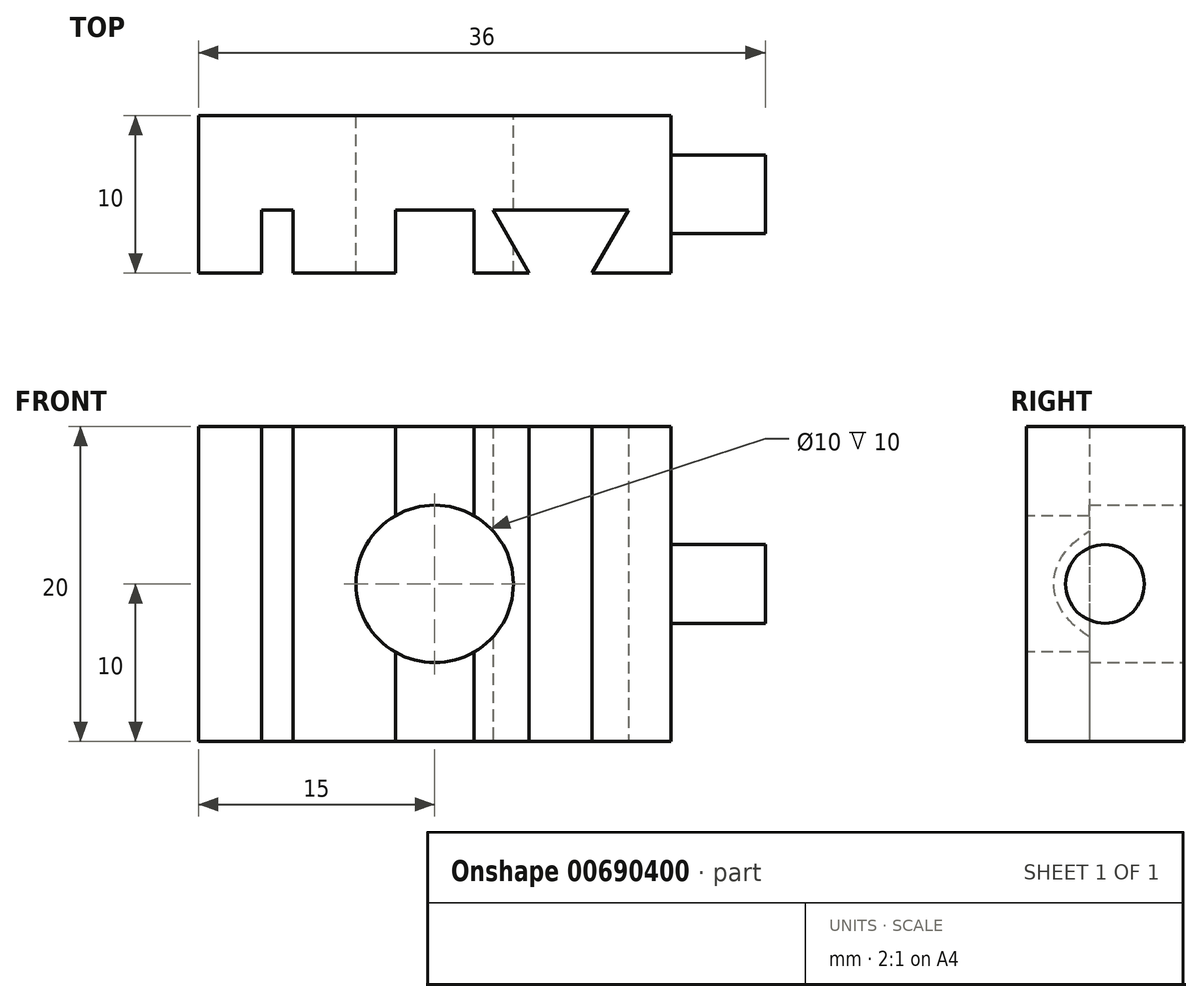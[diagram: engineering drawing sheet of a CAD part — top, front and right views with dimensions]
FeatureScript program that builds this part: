
annotation { "Feature Type Name" : "Feature", "Feature Type Description" : "" }
export const myFeature = defineFeature(function(context is Context, id is Id, definition is map)
    precondition{}
    {
        {
            var Q0;
            Q0=qCreatedBy(makeId("Front.planeOp"),FACE);
            var sketch = newSketch(context, id + "F0", { "sketchPlane" : qUnion([Q0])});
            skLineSegment(sketch, "E0.bottom", {"start": v(15, -10) * mm, "end": v(-15, -10) * mm});
            skLineSegment(sketch, "E0.top", {"start": v(15, 10) * mm, "end": v(-15, 10) * mm});
            skLineSegment(sketch, "E0.left", {"start": v(15, -10) * mm, "end": v(15, 10) * mm});
            skLineSegment(sketch, "E0.right", {"start": v(-15, -10) * mm, "end": v(-15, 10) * mm});
            skPoint(sketch, "E0.middle", {"position": v(0, 0) * mm});
            skCircle(sketch, "E1", {"center": v(0, 0) * mm, "radius": 5 * mm});
            skSolve(sketch);
        }
        {
            var Q0;
            Q0=makeQuery(id+"F0.imprint","IMPRINT",FACE,{"disambiguationData":[TD([[makeQuery(id+"F0.imprint","IMPRINT",EDGE,{"derivedFrom":sQuery(id+"F0.wireOp",EDGE,"E0.bottom")}),-1.0]])]});
            extrude(context, id + "F1", {"entities" : qUnion([Q0]), "depth" : 10 * mm, "offsetDistance" : 25 * mm});
        }
        {
            var Q0;
            Q0=makeQuery(id+"F1.opExtrude","CAP_FACE",FACE,{"disambiguationData":[OSD([sQuery(id+"F0.wireOp",EDGE,"E0.bottom"),sQuery(id+"F0.wireOp",EDGE,"E0.top"),sQuery(id+"F0.wireOp",EDGE,"E0.left"),sQuery(id+"F0.wireOp",EDGE,"E0.right"),sQuery(id+"F0.wireOp",EDGE,"E1")])],"isStart":false});
            var sketch = newSketch(context, id + "F2", { "sketchPlane" : qUnion([Q0])});
            skLineSegment(sketch, "E2.bottom", {"start": v(-11, 10) * mm, "end": v(-9, 10) * mm});
            skLineSegment(sketch, "E2.top", {"start": v(-11, -10) * mm, "end": v(-9, -10) * mm});
            skLineSegment(sketch, "E2.left", {"start": v(-11, 10) * mm, "end": v(-11, -10) * mm});
            skLineSegment(sketch, "E2.right", {"start": v(-9, 10) * mm, "end": v(-9, -10) * mm});
            skLineSegment(sketch, "E3", {"start": v(-2.5, 10) * mm, "end": v(-2.5, -10) * mm});
            skLineSegment(sketch, "E4", {"start": v(-2.5, -10) * mm, "end": v(2.5, -10) * mm});
            skLineSegment(sketch, "E5", {"start": v(2.5, -10) * mm, "end": v(2.5, 10) * mm});
            skLineSegment(sketch, "E6", {"start": v(2.5, 10) * mm, "end": v(-2.5, 10) * mm});
            skLineSegment(sketch, "E7", {"start": v(0, 10) * mm, "end": v(0, -10) * mm, "construction": true});
            skSolve(sketch);
        }
        {
            var Q0;
            Q0=makeQuery(id+"F2.imprint","IMPRINT",FACE,{"disambiguationData":[TD([[makeQuery(id+"F2.imprint","IMPRINT",EDGE,{"derivedFrom":sQuery(id+"F2.wireOp",EDGE,"E2.bottom")}),1.0]])]});
            var Q1;
            {var subQ0=sQuery(id+"F2.wireOp",EDGE,"E6");Q1=makeQuery(id+"F2.imprint","IMPRINT",FACE,{"disambiguationData":[TD([[makeQuery(id+"F2.imprint","IMPRINT",EDGE,{"derivedFrom":subQ0}),1.0]])]});}
            var Q2;
            {var subQ0=sQuery(id+"F2.wireOp",EDGE,"E4");Q2=makeQuery(id+"F2.imprint","IMPRINT",FACE,{"disambiguationData":[TD([[makeQuery(id+"F2.imprint","IMPRINT",EDGE,{"derivedFrom":subQ0}),-1.0]])]});}
            extrude(context, id + "F3", {"entities" : qUnion([Q0, Q1, Q2]), "operationType" : NewBodyOperationType.REMOVE, "oppositeDirection" : true, "depth" : 4 * mm, "offsetDistance" : 25 * mm});
        }
        {
            var Q0;
            Q0=makeQuery(id+"F1.opExtrude","SWEPT_FACE",FACE,{"disambiguationData":[OSD([sQuery(id+"F0.wireOp",EDGE,"E0.bottom")])]});
            var sketch = newSketch(context, id + "F4", { "sketchPlane" : qUnion([Q0])});
            skLineSegment(sketch, "E8", {"start": v(6, 10) * mm, "end": v(3.7, 6) * mm});
            skLineSegment(sketch, "E9", {"start": v(3.7, 6) * mm, "end": v(12.3, 6) * mm});
            skLineSegment(sketch, "E10", {"start": v(12.3, 6) * mm, "end": v(10, 10) * mm});
            skLineSegment(sketch, "E11", {"start": v(10, 10) * mm, "end": v(6, 10) * mm});
            skLineSegment(sketch, "E12", {"start": v(8, 6) * mm, "end": v(8, 10) * mm, "construction": true});
            skSolve(sketch);
        }
        {
            var Q0;
            Q0=makeQuery(id+"F4.imprint","IMPRINT",FACE,{"disambiguationData":[TD([[makeQuery(id+"F4.imprint","IMPRINT",EDGE,{"derivedFrom":sQuery(id+"F4.wireOp",EDGE,"E8")}),1.0]])]});
            extrude(context, id + "F5", {"entities" : qUnion([Q0]), "operationType" : NewBodyOperationType.REMOVE, "endBound" : BoundingType.UP_TO_NEXT, "oppositeDirection" : true, "depth" : 13 * mm, "offsetDistance" : 25 * mm});
        }
        {
            var Q0;
            Q0=makeQuery(id+"F1.opExtrude","SWEPT_FACE",FACE,{"disambiguationData":[OSD([sQuery(id+"F0.wireOp",EDGE,"E0.left")])]});
            var sketch = newSketch(context, id + "F6", { "sketchPlane" : qUnion([Q0])});
            skCircle(sketch, "E13", {"center": v(-5, 0) * mm, "radius": 2.5 * mm});
            skPoint(sketch, "E13.centerSnap0", {"position": v(-5, -10) * mm});
            skPoint(sketch, "E13.centerSnap1", {"position": v(-10, 0) * mm});
            skSolve(sketch);
        }
        {
            var Q0;
            Q0=makeQuery(id+"F6.imprint","IMPRINT",FACE,{"disambiguationData":[TD([[makeQuery(id+"F6.imprint","IMPRINT",EDGE,{"derivedFrom":sQuery(id+"F6.wireOp",EDGE,"E13")}),1.0]])]});
            extrude(context, id + "F7", {"entities" : qUnion([Q0]), "operationType" : NewBodyOperationType.ADD, "depth" : 6 * mm, "offsetDistance" : 25 * mm});
        }
    });
